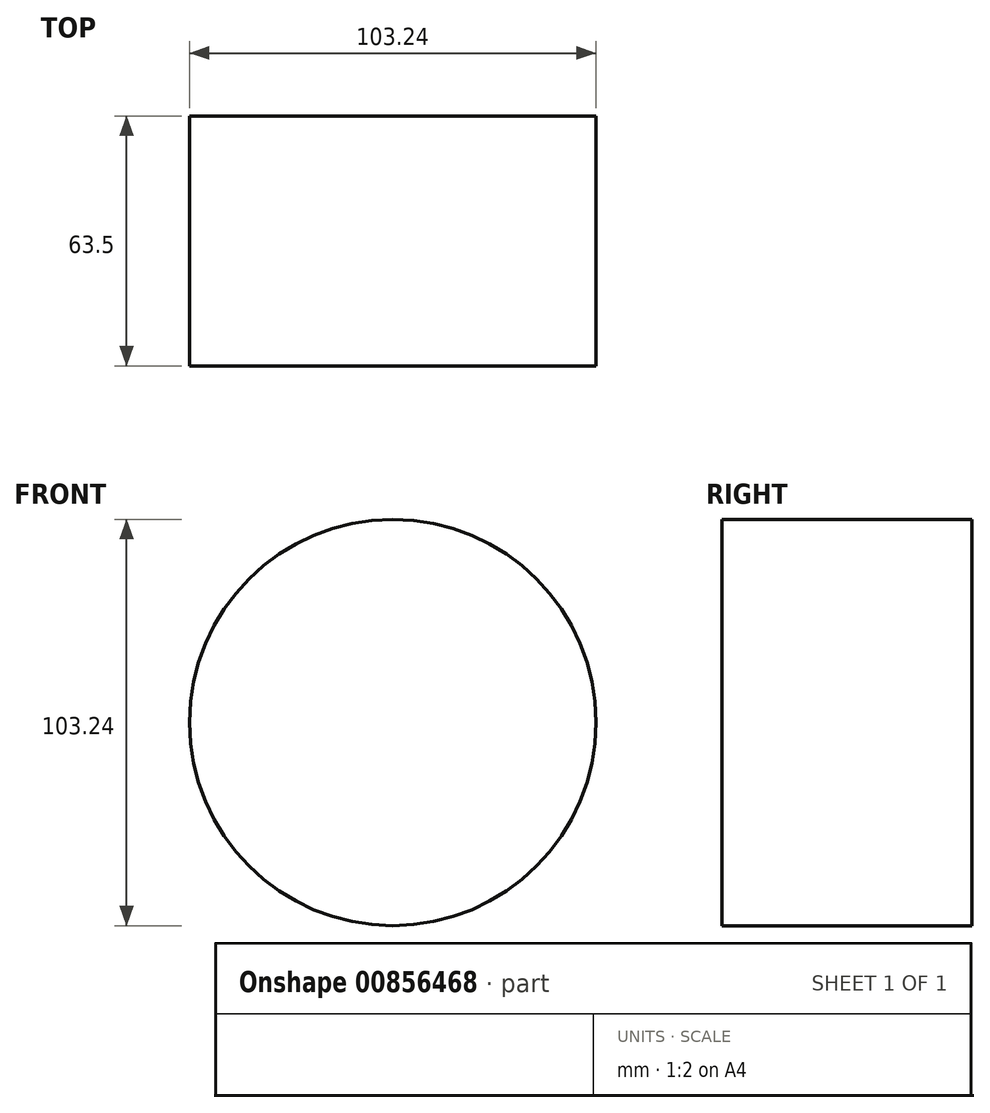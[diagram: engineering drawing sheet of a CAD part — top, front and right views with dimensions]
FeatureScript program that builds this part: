
annotation { "Feature Type Name" : "Feature", "Feature Type Description" : "" }
export const myFeature = defineFeature(function(context is Context, id is Id, definition is map)
    precondition{}
    {
        {
            var Q0;
            Q0=qCreatedBy(makeId("Front.planeOp"),FACE);
            var sketch = newSketch(context, id + "F0", { "sketchPlane" : qUnion([Q0])});
            skCircle(sketch, "E0", {"center": v(0, 0) * mm, "radius": 51.62 * mm});
            skSolve(sketch);
        }
        {
            var Q0;
            Q0 = qSketchRegion(id + "F0", true);
            extrude(context, id + "F1", {"entities" : qUnion([Q0]), "depth" : 63.5 * mm, "offsetDistance" : 25.4 * mm});
        }
    });
